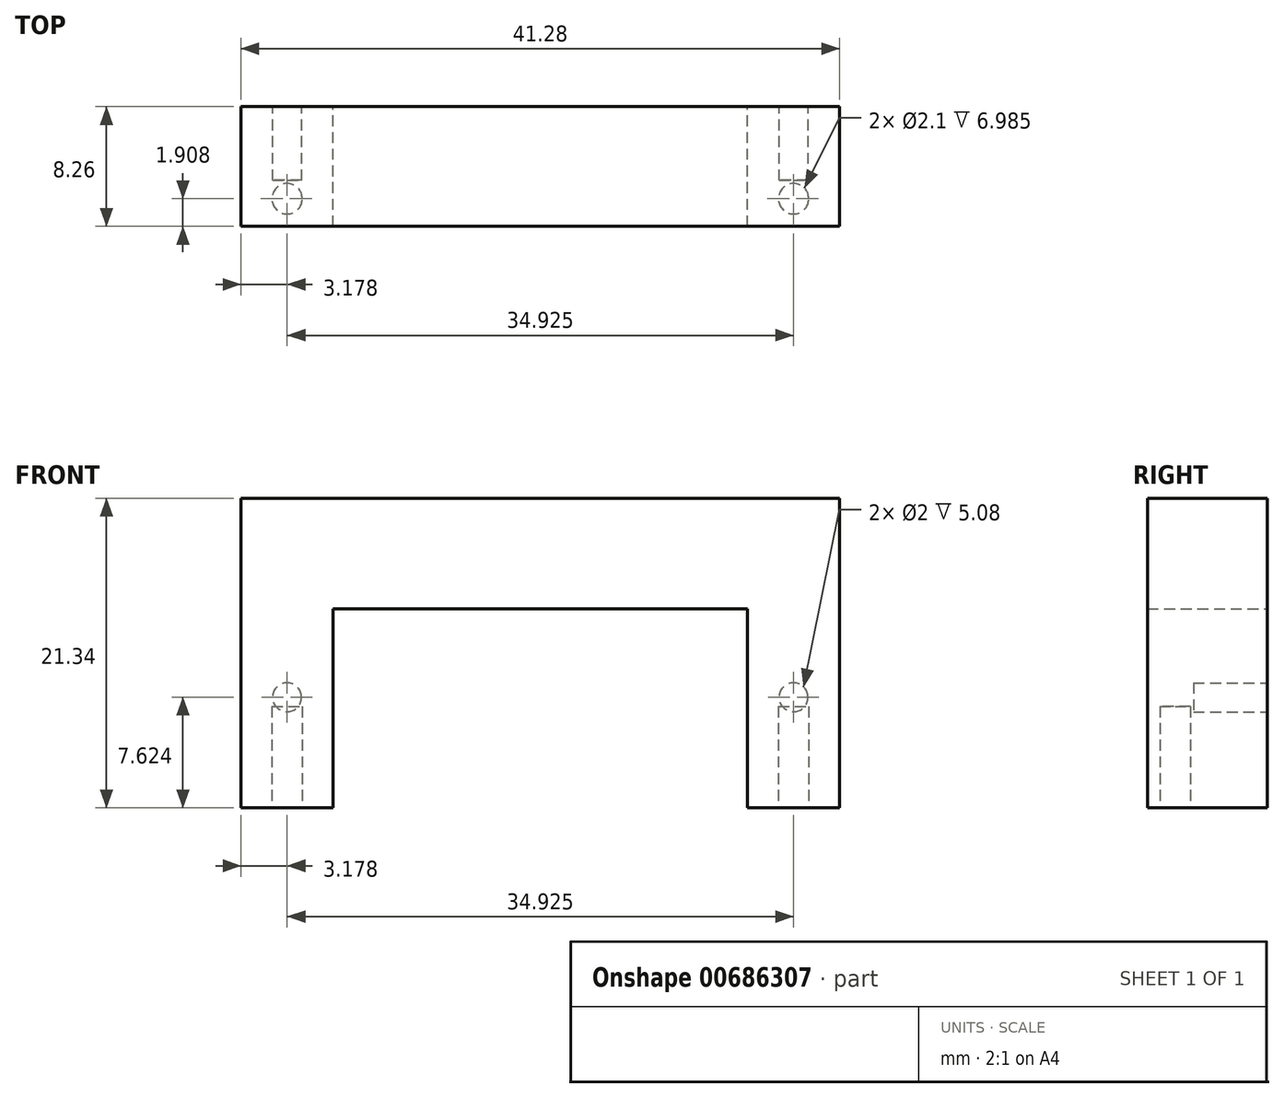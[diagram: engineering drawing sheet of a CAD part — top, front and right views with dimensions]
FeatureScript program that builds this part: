
annotation { "Feature Type Name" : "Feature", "Feature Type Description" : "" }
export const myFeature = defineFeature(function(context is Context, id is Id, definition is map)
    precondition{}
    {
        {
            var Q0;
            Q0=qCreatedBy(makeId("Front.planeOp"),FACE);
            var sketch = newSketch(context, id + "F0", { "sketchPlane" : qUnion([Q0])});
            skLineSegment(sketch, "E0", {"start": v(0, 0) * mm, "end": v(14.29, 0) * mm});
            skLineSegment(sketch, "E1", {"start": v(0, 0) * mm, "end": v(0, 11.27) * mm, "construction": true});
            skLineSegment(sketch, "E2", {"start": v(20.64, 7.62) * mm, "end": v(0, 7.62) * mm});
            skLineSegment(sketch, "E3", {"start": v(14.29, 0) * mm, "end": v(14.29, -13.72) * mm});
            skLineSegment(sketch, "E4", {"start": v(14.29, -13.72) * mm, "end": v(20.64, -13.72) * mm});
            skLineSegment(sketch, "E5", {"start": v(20.64, -13.72) * mm, "end": v(20.64, 7.62) * mm});
            skLineSegment(sketch, "E6.MirrorCS", {"start": v(-20.64, 7.62) * mm, "end": v(0, 7.62) * mm});
            skLineSegment(sketch, "E7.MirrorCS", {"start": v(-20.64, -13.72) * mm, "end": v(-20.64, 7.62) * mm});
            skLineSegment(sketch, "E8.MirrorCS", {"start": v(-14.29, -13.72) * mm, "end": v(-20.64, -13.72) * mm});
            skLineSegment(sketch, "E9.MirrorCS", {"start": v(0, 0) * mm, "end": v(-14.29, 0) * mm});
            skLineSegment(sketch, "E10.MirrorCS", {"start": v(-14.29, 0) * mm, "end": v(-14.29, -13.72) * mm});
            skSolve(sketch);
        }
        {
            var Q0;
            Q0=qSketchRegion(id+"F0",true);
            extrude(context, id + "F1", {"entities" : qUnion([Q0]), "endBound" : BoundingType.SYMMETRIC, "depth" : 21.34 * mm, "offsetDistance" : 25.4 * mm});
        }
        {
            var Q0;
            Q0=qCreatedBy(makeId("Right.planeOp"),FACE);
            var sketch = newSketch(context, id + "F2", { "sketchPlane" : qUnion([Q0])});
            skLineSegment(sketch, "E11", {"start": v(0, 0) * mm, "end": v(0, 21.33) * mm, "construction": true});
            skLineSegment(sketch, "E12.0", {"start": v(10.67, -13.72) * mm, "end": v(10.67, 0) * mm});
            skLineSegment(sketch, "E13", {"start": v(8.13, -13.72) * mm, "end": v(8.13, 0) * mm});
            skLineSegment(sketch, "E14", {"start": v(8.13, 0) * mm, "end": v(10.67, 0) * mm});
            skLineSegment(sketch, "E15", {"start": v(10.67, 0) * mm, "end": v(10.67, -13.72) * mm});
            skLineSegment(sketch, "E16", {"start": v(-0.13, -13.72) * mm, "end": v(-0.13, 0) * mm});
            skLineSegment(sketch, "E17.0", {"start": v(-10.67, -13.72) * mm, "end": v(-10.67, 0) * mm});
            skLineSegment(sketch, "E18", {"start": v(-0.13, 0) * mm, "end": v(-10.67, 0) * mm});
            skLineSegment(sketch, "E19", {"start": v(-10.67, 0) * mm, "end": v(-10.67, -13.72) * mm});
            skLineSegment(sketch, "E20", {"start": v(-0.13, -13.72) * mm, "end": v(-10.67, -13.72) * mm});
            skLineSegment(sketch, "E21", {"start": v(8.13, -13.72) * mm, "end": v(10.67, -13.72) * mm});
            skSolve(sketch);
        }
        {
            var Q0;
            Q0=qSketchRegion(id+"F2",true);
            extrude(context, id + "F3", {"entities" : qUnion([Q0]), "operationType" : NewBodyOperationType.REMOVE, "endBound" : BoundingType.THROUGH_ALL, "oppositeDirection" : true, "depth" : 25.4 * mm, "offsetDistance" : 25.4 * mm, "hasSecondDirection" : true, "secondDirectionBound" : SecondDirectionBoundingType.THROUGH_ALL, "secondDirectionOppositeDirection" : false, "secondDirectionDepth" : 25.4 * mm});
        }
        {
            var Q0;
            Q0=makeQuery(id+"F3.boolean.opBoolean","COPY",FACE,{"disambiguationData":[TD([makeQuery(id+"F1.opExtrude","SWEPT_FACE",FACE,{"disambiguationData":[OSD([sQuery(id+"F0.wireOp",EDGE,"E3")])]})])],"derivedFrom":makeQuery(id+"F3.opExtrude","SWEPT_FACE",FACE,{"disambiguationData":[OSD([sQuery(id+"F2.wireOp",EDGE,"E13")])]})});
            var sketch = newSketch(context, id + "F4", { "sketchPlane" : qUnion([Q0])});
            skPoint(sketch, "E22.0", {"position": v(-17.46, -13.72) * mm});
            skCircle(sketch, "E23", {"center": v(-17.46, -6.1) * mm, "radius": 1 * mm});
            skLineSegment(sketch, "E24", {"start": v(0, 0) * mm, "end": v(0, 4.68) * mm, "construction": true});
            skCircle(sketch, "E25.MirrorC", {"center": v(17.46, -6.1) * mm, "radius": 1 * mm});
            skSolve(sketch);
        }
        {
            var Q0;
            Q0=qSketchRegion(id+"F4",true);
            extrude(context, id + "F5", {"entities" : qUnion([Q0]), "operationType" : NewBodyOperationType.REMOVE, "oppositeDirection" : true, "depth" : 5.08 * mm, "offsetDistance" : 25.4 * mm});
        }
        {
            var Q0;
            Q0=makeQuery(id+"F1.opExtrude","SWEPT_FACE",FACE,{"disambiguationData":[OSD([sQuery(id+"F0.wireOp",EDGE,"E4")])]});
            var sketch = newSketch(context, id + "F6", { "sketchPlane" : qUnion([Q0])});
            skCircle(sketch, "E26", {"center": v(-17.46, -1.78) * mm, "radius": 1.05 * mm});
            skLineSegment(sketch, "E27", {"start": v(0, 0) * mm, "end": v(0, 7.66) * mm, "construction": true});
            skCircle(sketch, "E28.MirrorC", {"center": v(17.46, -1.78) * mm, "radius": 1.05 * mm});
            skSolve(sketch);
        }
        {
            var Q0;
            Q0=qSketchRegion(id+"F6",true);
            extrude(context, id + "F7", {"entities" : qUnion([Q0]), "operationType" : NewBodyOperationType.REMOVE, "oppositeDirection" : true, "depth" : 7 * mm, "offsetDistance" : 25.4 * mm});
        }
        {
            var Q0;
            Q0=qCreatedBy(makeId("Right.planeOp"),FACE);
            var sketch = newSketch(context, id + "F8", { "sketchPlane" : qUnion([Q0])});
            skLineSegment(sketch, "E29.0", {"start": v(-0.13, 0) * mm, "end": v(-0.13, -13.72) * mm, "construction": true});
            skLineSegment(sketch, "E30.0", {"start": v(8.13, 0) * mm, "end": v(8.13, -13.72) * mm, "construction": true});
            skLineSegment(sketch, "E31", {"start": v(-0.13, 0) * mm, "end": v(-0.13, 8.62) * mm});
            skLineSegment(sketch, "E32", {"start": v(8.13, 0) * mm, "end": v(12.4, 0) * mm});
            skLineSegment(sketch, "E33", {"start": v(-0.13, 0) * mm, "end": v(-11.57, 0) * mm});
            skLineSegment(sketch, "E34", {"start": v(-11.57, 0) * mm, "end": v(-11.57, 8.62) * mm});
            skLineSegment(sketch, "E35", {"start": v(-11.57, 8.62) * mm, "end": v(-0.13, 8.62) * mm});
            skLineSegment(sketch, "E36", {"start": v(12.4, 0) * mm, "end": v(12.4, 8.62) * mm});
            skLineSegment(sketch, "E37", {"start": v(8.13, 0) * mm, "end": v(8.13, 8.62) * mm});
            skLineSegment(sketch, "E38.trimOffspring", {"start": v(8.13, 8.62) * mm, "end": v(12.4, 8.62) * mm});
            skSolve(sketch);
        }
        {
            var Q0;
            Q0=qSketchRegion(id+"F8",true);
            extrude(context, id + "F9", {"entities" : qUnion([Q0]), "operationType" : NewBodyOperationType.REMOVE, "endBound" : BoundingType.THROUGH_ALL, "depth" : 25 * mm, "offsetDistance" : 25 * mm, "hasSecondDirection" : true, "secondDirectionBound" : SecondDirectionBoundingType.THROUGH_ALL, "secondDirectionOppositeDirection" : true, "secondDirectionDepth" : 25 * mm});
        }
    });
